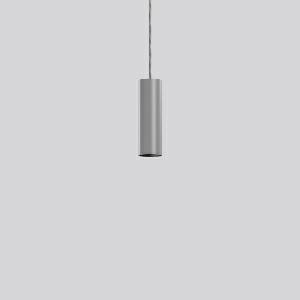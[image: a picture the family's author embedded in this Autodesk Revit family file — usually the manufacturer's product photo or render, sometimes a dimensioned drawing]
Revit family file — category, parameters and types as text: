
# Revit family: deecos_p_micro_911490_004_068f
name_source: partatom
category: Lighting Fixtures
units: mm (PartAtom-declared; Revit-internal decimal feet)

## family parameters
Cut with Voids When Loaded = No
Host = Face
Light Source = No
Part Type = Normal
Room Calculation Point = No
Round Connector Dimension = Use Diameter
Shared = No

## types (1)
- DEECOS P micro (1 x LED Modul 927, 1150 lm, 2700)
    Apparent Load = 16 VA
    CIE Flux Codes = 92 99 100 100 100
    Color Rendering = 92
    Color Temperature = 2700
    Default Elevation = 1800 mm
    Description = Series: DEECOS P micro
Cylindrical pendant luminaire. Housing: die-cast aluminium, powder-coated. Canopy made of powder-coated sheet steel with magnetic attachment. Optical assembly with lens made of plastic (polycarbonate) for the best homogeneous light distribution - can be changed without tools. Black plastic ring and recessed LED to prevent glare from the side. Best colour rendering index Ra>90. Transparent suspension cable 3 m, can be shortened. High quality converter without flickering and stroboscopic effect. 
Colour: silver
Diameter: 60 mm
Height: 190 mm
Suspension length: 3000 mm
Lamp: LED
Socket: without socket
Colour temperature: 2700K
Colour rendering index (CRI): 92
System power: 16 W
Rated luminous flux: 1150 lm
Luminous efficiency: 72 lm/W
Control gear: Regulated power supply
Protection class: I
Type of protection: IP 20
    Height = 190 mm  [stored 0.62336 ft]
    Lamp = 1 x LED Modul 927
    Lamp Light Flux = 1150 lm
    Lamp count = 1
    Length = 60 mm  [stored 0.19685 ft]
    Lifetime = 50000 h
    Luminous efficacy = 72 lm/W
    Manufacturer = RZB
    ModVariant = No
    Model = 911490.004
    Mounting Place = Ceiling
    Mounting Type = Pendant
    Number of Poles = 1
    OnlyDefault = Yes
    Power Factor = 1
    Product Name = DEECOS P micro
    Product group = Pendant luminaires
    ProductGroupID = 902
    Protection Class = Protection class I
    Protection Degree = Degree of protection
    RLX_Detail_Level = 1
    RLX_Emergency_Light_Flux = 0 lm
    RLX_Emergency_Type = 0
    RLX_Emergency_Type_DB = No
    RlxData = <blob elided: 31585 chars, md5=3eb1e530>
    Socket = socket
    Standby Power = 0 W
    System Light Flux = 1150 lm
    System Power = 16 W
    Type Comments = Product without accessories
    Type Image = 911489.004.jpg
    URL = http://relux.com
    VarID = ---
    Voltage = 0 V
    Weight = 0.00 kg
    Width = 0 mm  [stored 0 ft]

note: [stored X ft] marks values corroborated as IEEE doubles in the binary element streams (Revit-internal decimal feet)

## geometry (parser evidence)
native form markers: Blend x4, Sweep x12
no freeform markers — native parametric forms only
